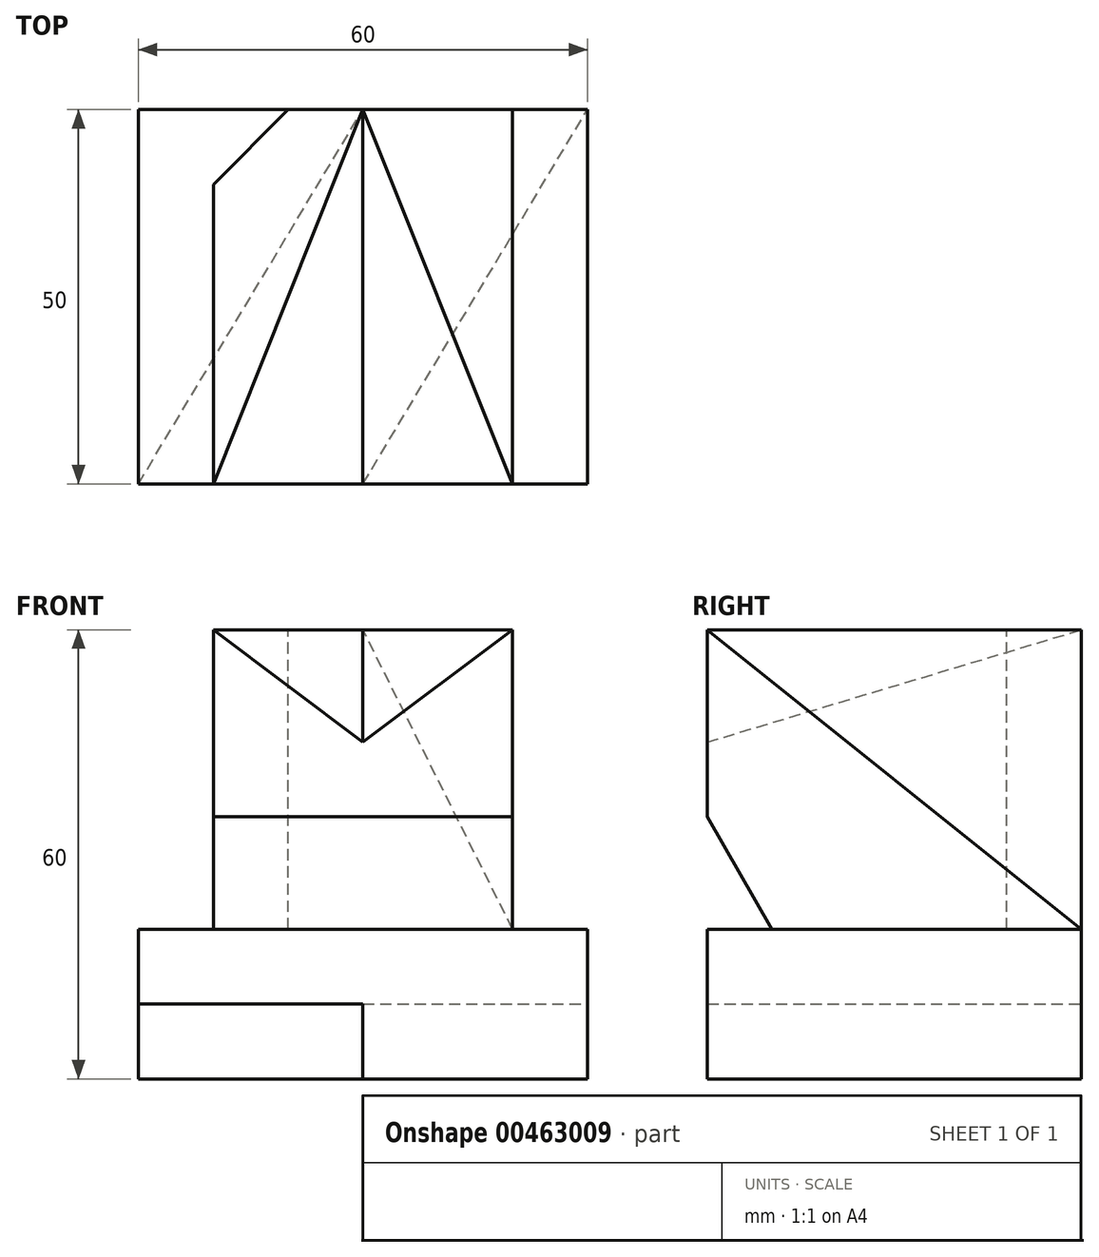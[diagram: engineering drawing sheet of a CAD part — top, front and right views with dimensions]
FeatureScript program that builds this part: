
annotation { "Feature Type Name" : "Feature", "Feature Type Description" : "" }
export const myFeature = defineFeature(function(context is Context, id is Id, definition is map)
    precondition{}
    {
        {
            var Q0;
            Q0=qCreatedBy(makeId("Top.planeOp"),FACE);
            var sketch = newSketch(context, id + "F0", { "sketchPlane" : qUnion([Q0])});
            skLineSegment(sketch, "E0.bottom", {"start": v(0, 0) * mm, "end": v(60, 0) * mm});
            skLineSegment(sketch, "E0.top", {"start": v(0, 50) * mm, "end": v(60, 50) * mm});
            skLineSegment(sketch, "E0.left", {"start": v(0, 0) * mm, "end": v(0, 50) * mm});
            skLineSegment(sketch, "E0.right", {"start": v(60, 0) * mm, "end": v(60, 50) * mm});
            skSolve(sketch);
        }
        {
            var Q0;
            Q0 = qSketchRegion(id + "F0", true);
            extrude(context, id + "F1", {"entities" : qUnion([Q0]), "depth" : 60 * mm});
        }
        {
            var Q0;
            Q0=makeQuery(id+"F1.opExtrude","CAP_FACE",FACE,{"disambiguationData":[OSD([sQuery(id+"F0.wireOp",EDGE,"E0.bottom"),sQuery(id+"F0.wireOp",EDGE,"E0.top"),sQuery(id+"F0.wireOp",EDGE,"E0.left"),sQuery(id+"F0.wireOp",EDGE,"E0.right")])],"isStart":false});
            var sketch = newSketch(context, id + "F2", { "sketchPlane" : qUnion([Q0])});
            skLineSegment(sketch, "E1.bottom", {"start": v(0, 50) * mm, "end": v(10, 50) * mm});
            skLineSegment(sketch, "E1.top", {"start": v(0, 0) * mm, "end": v(10, 0) * mm});
            skLineSegment(sketch, "E1.left", {"start": v(0, 50) * mm, "end": v(0, 0) * mm});
            skLineSegment(sketch, "E1.right", {"start": v(10, 50) * mm, "end": v(10, 0) * mm});
            skSolve(sketch);
        }
        {
            var Q0;
            Q0 = qSketchRegion(id + "F2", true);
            extrude(context, id + "F3", {"entities" : qUnion([Q0]), "operationType" : NewBodyOperationType.REMOVE, "oppositeDirection" : true, "depth" : 40 * mm});
        }
        {
            var Q0;
            Q0=makeQuery(id+"F1.opExtrude","CAP_FACE",FACE,{"disambiguationData":[OSD([sQuery(id+"F0.wireOp",EDGE,"E0.bottom"),sQuery(id+"F0.wireOp",EDGE,"E0.top"),sQuery(id+"F0.wireOp",EDGE,"E0.left"),sQuery(id+"F0.wireOp",EDGE,"E0.right")])],"isStart":false});
            var sketch = newSketch(context, id + "F4", { "sketchPlane" : qUnion([Q0])});
            skLineSegment(sketch, "E2", {"start": v(10, 50) * mm, "end": v(20, 50) * mm});
            skLineSegment(sketch, "E3", {"start": v(20, 50) * mm, "end": v(10, 50) * mm});
            skLineSegment(sketch, "E4", {"start": v(10, 50) * mm, "end": v(10, 40) * mm});
            skLineSegment(sketch, "E5", {"start": v(10, 40) * mm, "end": v(20, 50) * mm});
            skSolve(sketch);
        }
        {
            var Q0;
            Q0 = qSketchRegion(id + "F4", true);
            extrude(context, id + "F5", {"entities" : qUnion([Q0]), "operationType" : NewBodyOperationType.REMOVE, "oppositeDirection" : true, "depth" : 40 * mm});
        }
        {
            var Q0;
            Q0=makeQuery(id+"F1.opExtrude","CAP_FACE",FACE,{"disambiguationData":[OSD([sQuery(id+"F0.wireOp",EDGE,"E0.bottom"),sQuery(id+"F0.wireOp",EDGE,"E0.top"),sQuery(id+"F0.wireOp",EDGE,"E0.left"),sQuery(id+"F0.wireOp",EDGE,"E0.right")])],"isStart":false});
            var sketch = newSketch(context, id + "F6", { "sketchPlane" : qUnion([Q0])});
            skLineSegment(sketch, "E6.bottom", {"start": v(60, 50) * mm, "end": v(50, 50) * mm});
            skLineSegment(sketch, "E6.top", {"start": v(60, 0) * mm, "end": v(50, 0) * mm});
            skLineSegment(sketch, "E6.left", {"start": v(60, 50) * mm, "end": v(60, 0) * mm});
            skLineSegment(sketch, "E6.right", {"start": v(50, 50) * mm, "end": v(50, 0) * mm});
            skSolve(sketch);
        }
        {
            var Q0;
            Q0 = qSketchRegion(id + "F6", true);
            extrude(context, id + "F7", {"entities" : qUnion([Q0]), "operationType" : NewBodyOperationType.REMOVE, "oppositeDirection" : true, "depth" : 40 * mm});
        }
        {
            var Q0;
            Q0=makeQuery(id+"F1.opExtrude","CAP_FACE",FACE,{"disambiguationData":[OSD([sQuery(id+"F0.wireOp",EDGE,"E0.bottom"),sQuery(id+"F0.wireOp",EDGE,"E0.top"),sQuery(id+"F0.wireOp",EDGE,"E0.left"),sQuery(id+"F0.wireOp",EDGE,"E0.right")])],"isStart":false});
            var sketch = newSketch(context, id + "F8", { "sketchPlane" : qUnion([Q0])});
            skLineSegment(sketch, "E7", {"start": v(10, 0) * mm, "end": v(30, 0) * mm});
            skLineSegment(sketch, "E8", {"start": v(30, 0) * mm, "end": v(50, 0) * mm});
            skLineSegment(sketch, "E9", {"start": v(50, 0) * mm, "end": v(30, 50) * mm});
            skLineSegment(sketch, "E10", {"start": v(30, 50) * mm, "end": v(10, 0) * mm});
            skSolve(sketch);
        }
        {
            var Q0;
            Q0=makeQuery(id+"F1.opExtrude","SWEPT_FACE",FACE,{"disambiguationData":[OSD([sQuery(id+"F0.wireOp",EDGE,"E0.bottom")])]});
            var sketch = newSketch(context, id + "F9", { "sketchPlane" : qUnion([Q0])});
            skLineSegment(sketch, "E11", {"start": v(10, 60) * mm, "end": v(30, 45) * mm});
            skLineSegment(sketch, "E12", {"start": v(30, 45) * mm, "end": v(50, 60) * mm});
            skSolve(sketch);
        }
        {
            var Q0;
            Q0=makeQuery(id+"F7.boolean.opBoolean","COPY",FACE,{"derivedFrom":makeQuery(id+"F7.opExtrude","SWEPT_FACE",FACE,{"disambiguationData":[OSD([sQuery(id+"F6.wireOp",EDGE,"E6.right")])]})});
            var Q1;
            Q1=sQuery(id+"F9.wireOp",VERTEX,"E12.start");
            cPlane(context, id + "F10", {"entities" : qUnion([Q0, Q1]), "cplaneType" : CPlaneType.PLANE_POINT, "offset" : 25 * mm, "width" : 150 * mm, "height" : 150 * mm});
        }
        {
            var Q0;
            Q0=qCreatedBy(id+"F10.planeOp",FACE);
            var sketch = newSketch(context, id + "F11", { "sketchPlane" : qUnion([Q0])});
            skLineSegment(sketch, "E13", {"start": v(0, 45) * mm, "end": v(50, 60) * mm});
            skSolve(sketch);
        }
        {
            var Q0;
            Q0=makeQuery(id+"F9.imprint","IMPRINT",FACE,{"disambiguationData":[TD([[makeQuery(id+"F9.imprint","IMPRINT",EDGE,{"derivedFrom":sQuery(id+"F9.wireOp",EDGE,"E11")}),1.0]])]});
            var Q1;
            Q1=sQuery(id+"F11.wireOp",EDGE,"E13");
            sweep(context, id + "F12", {"operationType" : NewBodyOperationType.REMOVE, "profiles" : qUnion([Q0]), "path" : qUnion([Q1])});
        }
        {
            var Q0;
            Q0=makeQuery(id+"F1.opExtrude","CAP_FACE",FACE,{"disambiguationData":[OSD([sQuery(id+"F0.wireOp",EDGE,"E0.bottom"),sQuery(id+"F0.wireOp",EDGE,"E0.top"),sQuery(id+"F0.wireOp",EDGE,"E0.left"),sQuery(id+"F0.wireOp",EDGE,"E0.right")])],"isStart":true});
            var sketch = newSketch(context, id + "F13", { "sketchPlane" : qUnion([Q0])});
            skLineSegment(sketch, "E14", {"start": v(0, 0) * mm, "end": v(30, 0) * mm});
            skLineSegment(sketch, "E15", {"start": v(60, -50) * mm, "end": v(30, -50) * mm});
            skLineSegment(sketch, "E16", {"start": v(30, 0) * mm, "end": v(60, -50) * mm});
            skLineSegment(sketch, "E17", {"start": v(0, 0) * mm, "end": v(30, -50) * mm});
            skSolve(sketch);
        }
        {
            var Q0;
            Q0 = qSketchRegion(id + "F13", true);
            extrude(context, id + "F14", {"entities" : qUnion([Q0]), "operationType" : NewBodyOperationType.REMOVE, "oppositeDirection" : true, "depth" : 10 * mm});
        }
        {
            var Q0;
            Q0=makeQuery(id+"F7.boolean.opBoolean","COPY",FACE,{"derivedFrom":makeQuery(id+"F7.opExtrude","SWEPT_FACE",FACE,{"disambiguationData":[OSD([sQuery(id+"F6.wireOp",EDGE,"E6.right")])]})});
            var sketch = newSketch(context, id + "F15", { "sketchPlane" : qUnion([Q0])});
            skLineSegment(sketch, "E18", {"start": v(0, 20) * mm, "end": v(0, 35) * mm});
            skLineSegment(sketch, "E19", {"start": v(0, 35) * mm, "end": v(8.66, 20) * mm});
            skLineSegment(sketch, "E20", {"start": v(0, 35) * mm, "end": v(0, 20) * mm});
            skLineSegment(sketch, "E21", {"start": v(0, 20) * mm, "end": v(8.66, 20) * mm});
            skSolve(sketch);
        }
        {
            var Q0;
            Q0 = qSketchRegion(id + "F15", true);
            extrude(context, id + "F16", {"entities" : qUnion([Q0]), "operationType" : NewBodyOperationType.REMOVE, "endBound" : BoundingType.THROUGH_ALL, "oppositeDirection" : true, "depth" : 25 * mm});
        }
        {
            var Q0;
            Q0=makeQuery(id+"F1.opExtrude","SWEPT_FACE",FACE,{"disambiguationData":[OSD([sQuery(id+"F0.wireOp",EDGE,"E0.top")])]});
            var sketch = newSketch(context, id + "F17", { "sketchPlane" : qUnion([Q0])});
            skLineSegment(sketch, "E22", {"start": v(-30, 60) * mm, "end": v(-50, 20) * mm});
            skSolve(sketch);
        }
        {
            var Q0;
            Q0=sQuery(id+"F17.wireOp",VERTEX,"E22.start");
            var Q1;
            Q1=sQuery(id+"F17.wireOp",VERTEX,"E22.end");
            var Q2;
            Q2=sQuery(id+"F8.wireOp",VERTEX,"E9.start");
            cPlane(context, id + "F18", {"entities" : qUnion([Q0, Q1, Q2]), "cplaneType" : CPlaneType.THREE_POINT, "offset" : 25 * mm, "width" : 150 * mm, "height" : 150 * mm});
        }
        {
            var Q0;
            Q0=qCreatedBy(id+"F18.planeOp",FACE);
            var sketch = newSketch(context, id + "F19", { "sketchPlane" : qUnion([Q0])});
            skLineSegment(sketch, "E23", {"start": v(-24.1, 31.3) * mm, "end": v(29, -4.47) * mm});
            skLineSegment(sketch, "E24", {"start": v(29, -4.47) * mm, "end": v(29, 40.25) * mm});
            skLineSegment(sketch, "E25", {"start": v(29, 40.25) * mm, "end": v(-24.1, 31.3) * mm});
            skSolve(sketch);
        }
        {
            var Q0;
            Q0 = qSketchRegion(id + "F19", true);
            extrude(context, id + "F20", {"entities" : qUnion([Q0]), "operationType" : NewBodyOperationType.REMOVE, "depth" : 25 * mm});
        }
    });
